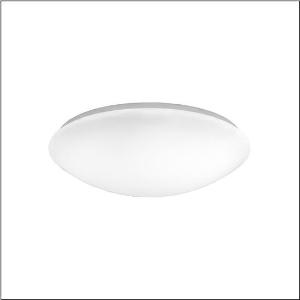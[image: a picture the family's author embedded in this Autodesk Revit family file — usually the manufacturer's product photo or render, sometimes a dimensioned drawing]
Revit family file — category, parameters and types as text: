
# Revit family: round_31_b_5pja212001a
name_source: partatom
category: Lighting Fixtures
units: mm (PartAtom-declared; Revit-internal decimal feet)

## family parameters
Cut with Voids When Loaded = No
Host = Face
Light Source = No
Part Type = Normal
Room Calculation Point = No
Round Connector Dimension = Use Diameter
Shared = No

## types (1)
- --- (1 x LED, 4700 lm, 39 W, 3000K)
    Apparent Load = 39 VA
    CIE Flux Codes = 42 71 89 88 100
    Color Rendering = 80
    Color Temperature = 3000K
    Default Elevation = 1800 mm
    Description = Round 31 B, wall and ceiling luminaire, primary optical cover: enclosure, of PMMA, light emission: direct distribution, primary light characteristic: symmetric, installation type: surface-mounted, LED, rated luminous flux: 4.700lm, luminous efficacy: 121lm/W, light colour: 830, colour temperature: 3000K, with terminal, 3+2-pole, max. 2.5mm², mains connection: 230V, AC, 50/60Hz, rated input power: 39W, luminaire housing, round, of steel, white, diameter: 464mm, height: 120mm, protection rating (complete): IP40, insulation class (complete): insulation class I (protective earthing), certification: CE, impact resistance: IK02, permissible operating ambient temperature: -20..+25°C, packaging unit: 1 piece
    Height = 120 mm
    Lamp = 1 x LED
    Lamp Light Flux = 4700 lm
    Lamp Power = 39 W
    Lamp count = 1
    Length = 464 mm
    Luminous efficacy = 121 lm/W
    Manufacturer = Siteco
    ModVariant = No
    Model = 5PJA212001A
    Mounting Place = Ceiling
    Mounting Type = Surface mounted
    Number of Poles = 1
    OnlyDefault = Yes
    Power Factor = 1
    Product Name = Round 31 B
    Product group = wall and ceiling luminaire
    ProductGroupID = 302
    Protection Class = Protection class I
    Protection Degree = IP 40
    RLX_Detail_Level = 1
    RLX_Emergency_Light_Flux = 0 lm
    RLX_Emergency_Type = 0
    RLX_Emergency_Type_DB = No
    RlxData = <blob elided: 13805 chars, md5=4fd6b8b3>
    Socket = socket
    Standby Power = 0 W
    System Light Flux = 4700 lm
    System Power = 39 W
    Type Comments = factory setting: luminous flux: 100 % | (ON | ON | ON) | 1050 mA
    Type Image = l_1258313.jpg
    URL = http://relux.com
    VarID = @adj_032375
    Voltage = 0 V
    Weight = 0.00 kg
    Width = 0 mm  [stored 0 ft]

note: [stored X ft] marks values corroborated as IEEE doubles in the binary element streams (Revit-internal decimal feet)

## geometry (parser evidence)
native form markers: Sweep x13
no freeform markers — native parametric forms only
